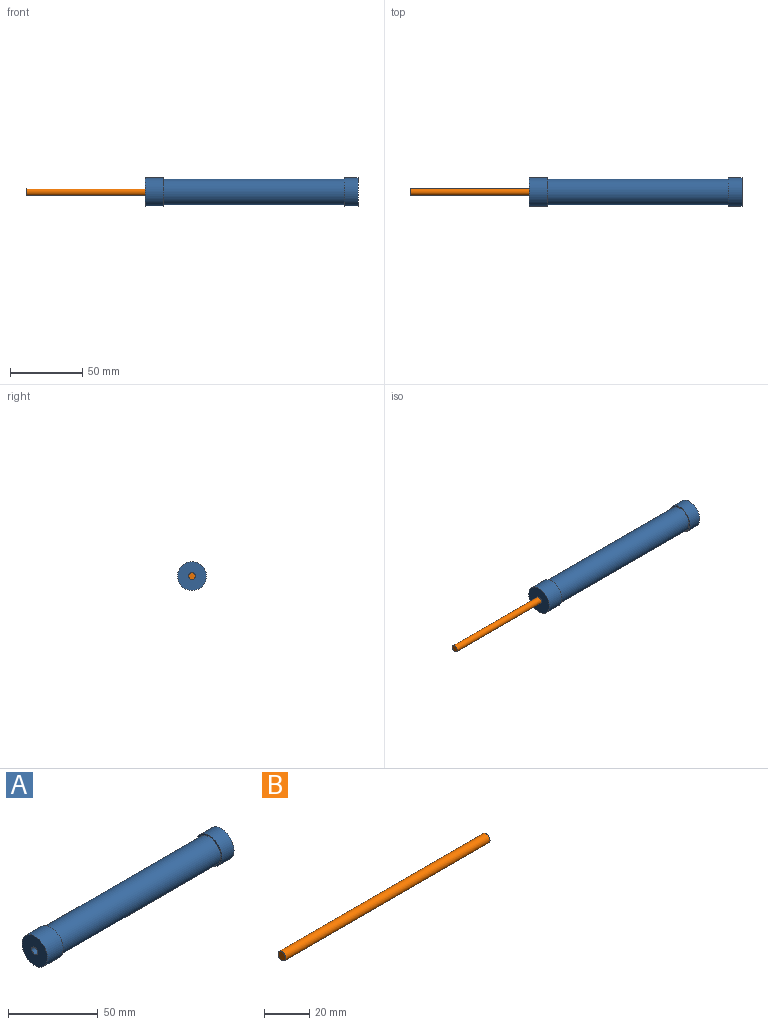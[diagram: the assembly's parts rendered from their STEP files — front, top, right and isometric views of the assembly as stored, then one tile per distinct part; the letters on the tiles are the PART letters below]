
ASSEMBLY  parts=2 mates=1
PART A: 9 faces, bbox 147.5x20x20 mm
  f0: cylinder r=9mm len=125.5mm, axis (-1,0,0), area 7096.9mm2, adj f1,f6
  f1: plane 20x20mm, normal (1,0,0), area 59.7mm2, adj f0,f2
  f2: cylinder r=10mm len=20mm, axis (-1,0,0), area 785.4mm2, adj f1,f3
  f3: plane 20x20mm, normal (-1,0,0), area 296.1mm2, adj f2,f8
  f4: plane 20x20mm, normal (1,0,0), area 314.2mm2, adj f5
  f5: cylinder r=10mm len=20mm, axis (-1,0,0), area 596.9mm2, adj f4,f6
  f6: plane 20x20mm, normal (-1,0,0), area 59.7mm2, adj f0,f5
  f7: cone r=0mm half-angle=59deg, axis (-1,0,0), area 21.1mm2, adj f8
  f8: cylinder r=2.4mm len=100mm, axis (-1,0,0), area 1508mm2, adj f3,f7
PART B: 3 faces, bbox 128x4.8x4.8 mm
  f0: plane 4.8x4.8mm, normal (1,0,0), area 18.1mm2, adj f1
  f1: cylinder r=2.4mm len=128mm, axis (1,0,0), area 1930.2mm2, adj f0,f2
  f2: plane 4.8x4.8mm, normal (-1,0,0), area 18.1mm2, adj f1
PLACE A t=(14.22,11.44,-5.15)mm fixed
PLACE B t=(59.67,11.44,-5.15)mm
MATE slider A.f0 <-> B.f1  axis (-1,0,0) through (14.22,11.44,4.85)mm
